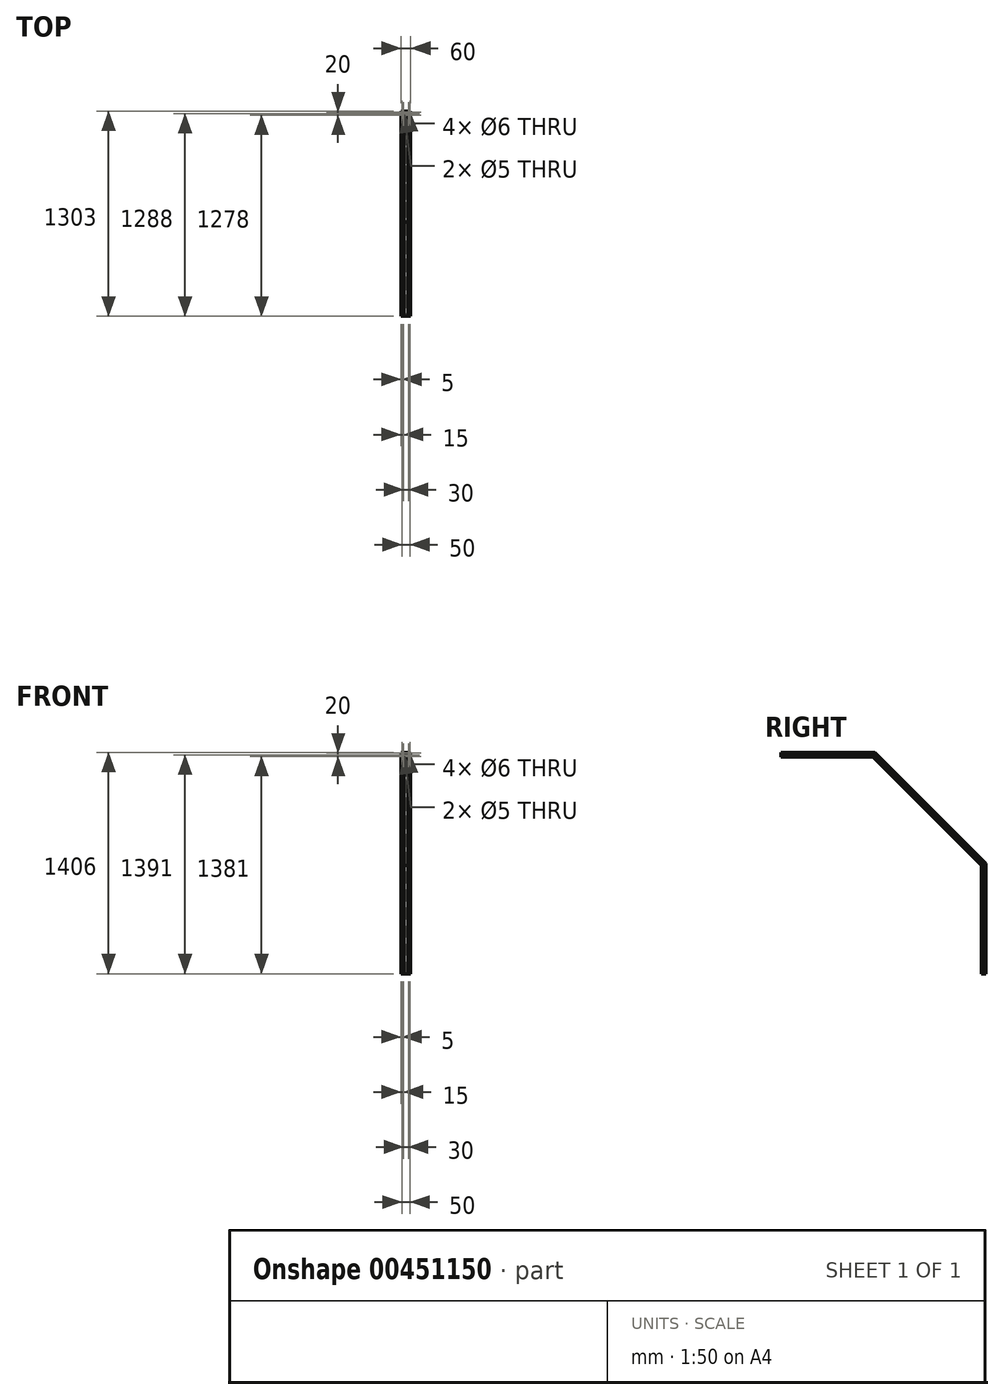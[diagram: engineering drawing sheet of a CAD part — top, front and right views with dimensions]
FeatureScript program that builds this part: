
annotation { "Feature Type Name" : "Feature", "Feature Type Description" : "" }
export const myFeature = defineFeature(function(context is Context, id is Id, definition is map)
    precondition{}
    {
        {
            var Q0;
            Q0=qCreatedBy(makeId("Top.planeOp"),FACE);
            var sketch = newSketch(context, id + "F0", { "sketchPlane" : qUnion([Q0])});
            skLineSegment(sketch, "E0.bottom", {"start": v(30, -15) * mm, "end": v(18.15, -15) * mm});
            skLineSegment(sketch, "E0.top", {"start": v(30, 15) * mm, "end": v(18.15, 15) * mm});
            skLineSegment(sketch, "E0.left", {"start": v(30, -15) * mm, "end": v(30, -3.15) * mm});
            skLineSegment(sketch, "E0.right", {"start": v(-30, -15) * mm, "end": v(-30, -3.15) * mm});
            skPoint(sketch, "E0.middle", {"position": v(0, 0) * mm});
            skLineSegment(sketch, "E1.left", {"start": v(-11.85, 12.5) * mm, "end": v(-11.85, 15) * mm});
            skLineSegment(sketch, "E1.right", {"start": v(-18.15, 12.5) * mm, "end": v(-18.15, 15) * mm});
            skPoint(sketch, "E1.middle", {"position": v(-15, 13.75) * mm});
            skLineSegment(sketch, "E2.bottom", {"start": v(-9.85, 12.5) * mm, "end": v(-11.85, 12.5) * mm});
            skLineSegment(sketch, "E2.left", {"start": v(-9.85, 12.5) * mm, "end": v(-9.85, 6.55) * mm});
            skLineSegment(sketch, "E2.right", {"start": v(-20.15, 12.5) * mm, "end": v(-20.15, 6.55) * mm});
            skPoint(sketch, "E2.middle", {"position": v(-15, 9.52) * mm});
            skArc(sketch, "E3", {"start": v(-20.15, 6.55) * mm, "mid": v(-15, 4.5) * mm, "end": v(-9.85, 6.55) * mm});
            skPoint(sketch, "E4.MirrorP", {"position": v(15, 9.52) * mm});
            skPoint(sketch, "E5.MirrorP", {"position": v(15, 13.75) * mm});
            skLineSegment(sketch, "E6.MirrorCS", {"start": v(11.85, 12.5) * mm, "end": v(11.85, 15) * mm});
            skLineSegment(sketch, "E7.MirrorCS", {"start": v(18.15, 12.5) * mm, "end": v(18.15, 15) * mm});
            skLineSegment(sketch, "E8.MirrorCS", {"start": v(9.85, 12.5) * mm, "end": v(11.85, 12.5) * mm});
            skLineSegment(sketch, "E9.MirrorCS", {"start": v(9.85, 12.5) * mm, "end": v(9.85, 6.55) * mm});
            skArc(sketch, "E10.MirrorCS", {"start": v(20.15, 6.55) * mm, "mid": v(15, 4.5) * mm, "end": v(9.85, 6.55) * mm});
            skLineSegment(sketch, "E11.MirrorCS", {"start": v(20.15, 12.5) * mm, "end": v(20.15, 6.55) * mm});
            skLineSegment(sketch, "E12.trimOffspring", {"start": v(-18.15, 12.5) * mm, "end": v(-20.15, 12.5) * mm});
            skLineSegment(sketch, "E13.trimOffspring", {"start": v(18.15, 12.5) * mm, "end": v(20.15, 12.5) * mm});
            skCircle(sketch, "E14", {"center": v(-15, 0) * mm, "radius": 2.5 * mm});
            skCircle(sketch, "E15", {"center": v(-25, 10) * mm, "radius": 3 * mm});
            skCircle(sketch, "E16.MirrorC", {"center": v(25, 10) * mm, "radius": 3 * mm});
            skCircle(sketch, "E17.MirrorC", {"center": v(25, -10) * mm, "radius": 3 * mm});
            skCircle(sketch, "E18.MirrorC", {"center": v(-25, -10) * mm, "radius": 3 * mm});
            skCircle(sketch, "E19.MirrorC", {"center": v(15, 0) * mm, "radius": 2.5 * mm});
            skLineSegment(sketch, "E20", {"start": v(-7, 12.5) * mm, "end": v(0, 12.5) * mm});
            skLineSegment(sketch, "E21", {"start": v(-7, 12.5) * mm, "end": v(-7, 7) * mm});
            skLineSegment(sketch, "E22", {"start": v(-10, 0) * mm, "end": v(-7, 7) * mm});
            skLineSegment(sketch, "E23.MirrorCS", {"start": v(10, 0) * mm, "end": v(7, 7) * mm});
            skLineSegment(sketch, "E24.MirrorCS", {"start": v(7, 12.5) * mm, "end": v(0, 12.5) * mm});
            skLineSegment(sketch, "E25.MirrorCS", {"start": v(7, 12.5) * mm, "end": v(7, 7) * mm});
            skLineSegment(sketch, "E26.MirrorCS", {"start": v(-18.15, -12.5) * mm, "end": v(-20.15, -12.5) * mm});
            skLineSegment(sketch, "E27.MirrorCS", {"start": v(-9.85, -12.5) * mm, "end": v(-11.85, -12.5) * mm});
            skLineSegment(sketch, "E28.MirrorCS", {"start": v(-9.85, -12.5) * mm, "end": v(-9.85, -6.55) * mm});
            skPoint(sketch, "E29.MirrorP", {"position": v(-15, -13.75) * mm});
            skPoint(sketch, "E30.MirrorP", {"position": v(-15, -9.52) * mm});
            skLineSegment(sketch, "E31.MirrorCS", {"start": v(-18.15, -12.5) * mm, "end": v(-18.15, -15) * mm});
            skLineSegment(sketch, "E32.MirrorCS", {"start": v(-20.15, -12.5) * mm, "end": v(-20.15, -6.55) * mm});
            skLineSegment(sketch, "E33.MirrorCS", {"start": v(-11.85, -12.5) * mm, "end": v(-11.85, -15) * mm});
            skArc(sketch, "E34.MirrorCS", {"start": v(-20.15, -6.55) * mm, "mid": v(-15, -4.5) * mm, "end": v(-9.85, -6.55) * mm});
            skLineSegment(sketch, "E35.MirrorCS", {"start": v(18.15, -12.5) * mm, "end": v(20.15, -12.5) * mm});
            skLineSegment(sketch, "E36.MirrorCS", {"start": v(9.85, -12.5) * mm, "end": v(11.85, -12.5) * mm});
            skPoint(sketch, "E37.MirrorP", {"position": v(15, -13.75) * mm});
            skPoint(sketch, "E38.MirrorP", {"position": v(15, -9.52) * mm});
            skLineSegment(sketch, "E39.MirrorCS", {"start": v(18.15, -12.5) * mm, "end": v(18.15, -15) * mm});
            skArc(sketch, "E40.MirrorCS", {"start": v(20.15, -6.55) * mm, "mid": v(15, -4.5) * mm, "end": v(9.85, -6.55) * mm});
            skLineSegment(sketch, "E41.MirrorCS", {"start": v(9.85, -12.5) * mm, "end": v(9.85, -6.55) * mm});
            skLineSegment(sketch, "E42.MirrorCS", {"start": v(11.85, -12.5) * mm, "end": v(11.85, -15) * mm});
            skLineSegment(sketch, "E43.MirrorCS", {"start": v(20.15, -12.5) * mm, "end": v(20.15, -6.55) * mm});
            skLineSegment(sketch, "E44.MirrorCS", {"start": v(10, 0) * mm, "end": v(7, -7) * mm});
            skLineSegment(sketch, "E45.MirrorCS", {"start": v(7, -12.5) * mm, "end": v(7, -7) * mm});
            skLineSegment(sketch, "E46.MirrorCS", {"start": v(7, -12.5) * mm, "end": v(0, -12.5) * mm});
            skLineSegment(sketch, "E47.MirrorCS", {"start": v(-7, -12.5) * mm, "end": v(0, -12.5) * mm});
            skLineSegment(sketch, "E48.MirrorCS", {"start": v(-10, 0) * mm, "end": v(-7, -7) * mm});
            skLineSegment(sketch, "E49.MirrorCS", {"start": v(-7, -12.5) * mm, "end": v(-7, -7) * mm});
            skLineSegment(sketch, "E50.left", {"start": v(-27.5, 3.15) * mm, "end": v(-30, 3.15) * mm});
            skLineSegment(sketch, "E50.right", {"start": v(-27.5, -3.15) * mm, "end": v(-30, -3.15) * mm});
            skLineSegment(sketch, "E51.bottom", {"start": v(-27.5, 5.15) * mm, "end": v(-27.5, 3.15) * mm});
            skLineSegment(sketch, "E51.left", {"start": v(-27.5, 5.15) * mm, "end": v(-21.55, 5.15) * mm});
            skLineSegment(sketch, "E51.right", {"start": v(-27.5, -5.15) * mm, "end": v(-21.55, -5.15) * mm});
            skArc(sketch, "E52", {"start": v(-21.55, -5.15) * mm, "mid": v(-19.5, 0) * mm, "end": v(-21.55, 5.15) * mm});
            skLineSegment(sketch, "E53.trimOffspring", {"start": v(-27.5, -3.15) * mm, "end": v(-27.5, -5.15) * mm});
            skArc(sketch, "E54.MirrorCS", {"start": v(21.55, -5.15) * mm, "mid": v(19.5, 0) * mm, "end": v(21.55, 5.15) * mm});
            skLineSegment(sketch, "E55.MirrorCS", {"start": v(27.5, -5.15) * mm, "end": v(21.55, -5.15) * mm});
            skLineSegment(sketch, "E56.MirrorCS", {"start": v(27.5, -3.15) * mm, "end": v(30, -3.15) * mm});
            skLineSegment(sketch, "E57.MirrorCS", {"start": v(27.5, 5.15) * mm, "end": v(27.5, 3.15) * mm});
            skLineSegment(sketch, "E58.MirrorCS", {"start": v(27.5, 3.15) * mm, "end": v(30, 3.15) * mm});
            skLineSegment(sketch, "E59.MirrorCS", {"start": v(27.5, 5.15) * mm, "end": v(21.55, 5.15) * mm});
            skLineSegment(sketch, "E60.MirrorCS", {"start": v(27.5, -3.15) * mm, "end": v(27.5, -5.15) * mm});
            skLineSegment(sketch, "E61.trimOffspring", {"start": v(30, 3.15) * mm, "end": v(30, 15) * mm});
            skLineSegment(sketch, "E62.trimOffspring", {"start": v(11.85, -15) * mm, "end": v(-11.85, -15) * mm});
            skLineSegment(sketch, "E63.trimOffspring", {"start": v(11.85, 15) * mm, "end": v(-11.85, 15) * mm});
            skLineSegment(sketch, "E64.trimOffspring", {"start": v(-18.15, -15) * mm, "end": v(-30, -15) * mm});
            skLineSegment(sketch, "E65.trimOffspring", {"start": v(-30, 3.15) * mm, "end": v(-30, 15) * mm});
            skLineSegment(sketch, "E66.trimOffspring", {"start": v(-18.15, 15) * mm, "end": v(-30, 15) * mm});
            skSolve(sketch);
        }
        {
            var Q0;
            Q0=qCreatedBy(makeId("Right.planeOp"),FACE);
            var sketch = newSketch(context, id + "F1", { "sketchPlane" : qUnion([Q0])});
            skLineSegment(sketch, "E67", {"start": v(-15, 0) * mm, "end": v(-15, 688) * mm});
            skLineSegment(sketch, "E68", {"start": v(-15, 688) * mm, "end": v(-703, 1376) * mm});
            skPoint(sketch, "E69.visualSharp", {"position": v(-15, 688) * mm});
            skLineSegment(sketch, "E70", {"start": v(-703, 1376) * mm, "end": v(-1288, 1376) * mm});
            skPoint(sketch, "E71.visualSharp", {"position": v(-703, 1376) * mm});
            skSolve(sketch);
        }
        {
            var Q0;
            Q0=qSketchRegion(id+"F0",true);
            var Q1;
            Q1=qConstructionFilter(qBodyType(qCreatedBy(id+"F1",EDGE),BodyType.WIRE),ConstructionObject.NO);
            sweep(context, id + "F2", {"profiles" : qUnion([Q0]), "path" : qUnion([Q1])});
        }
    });
